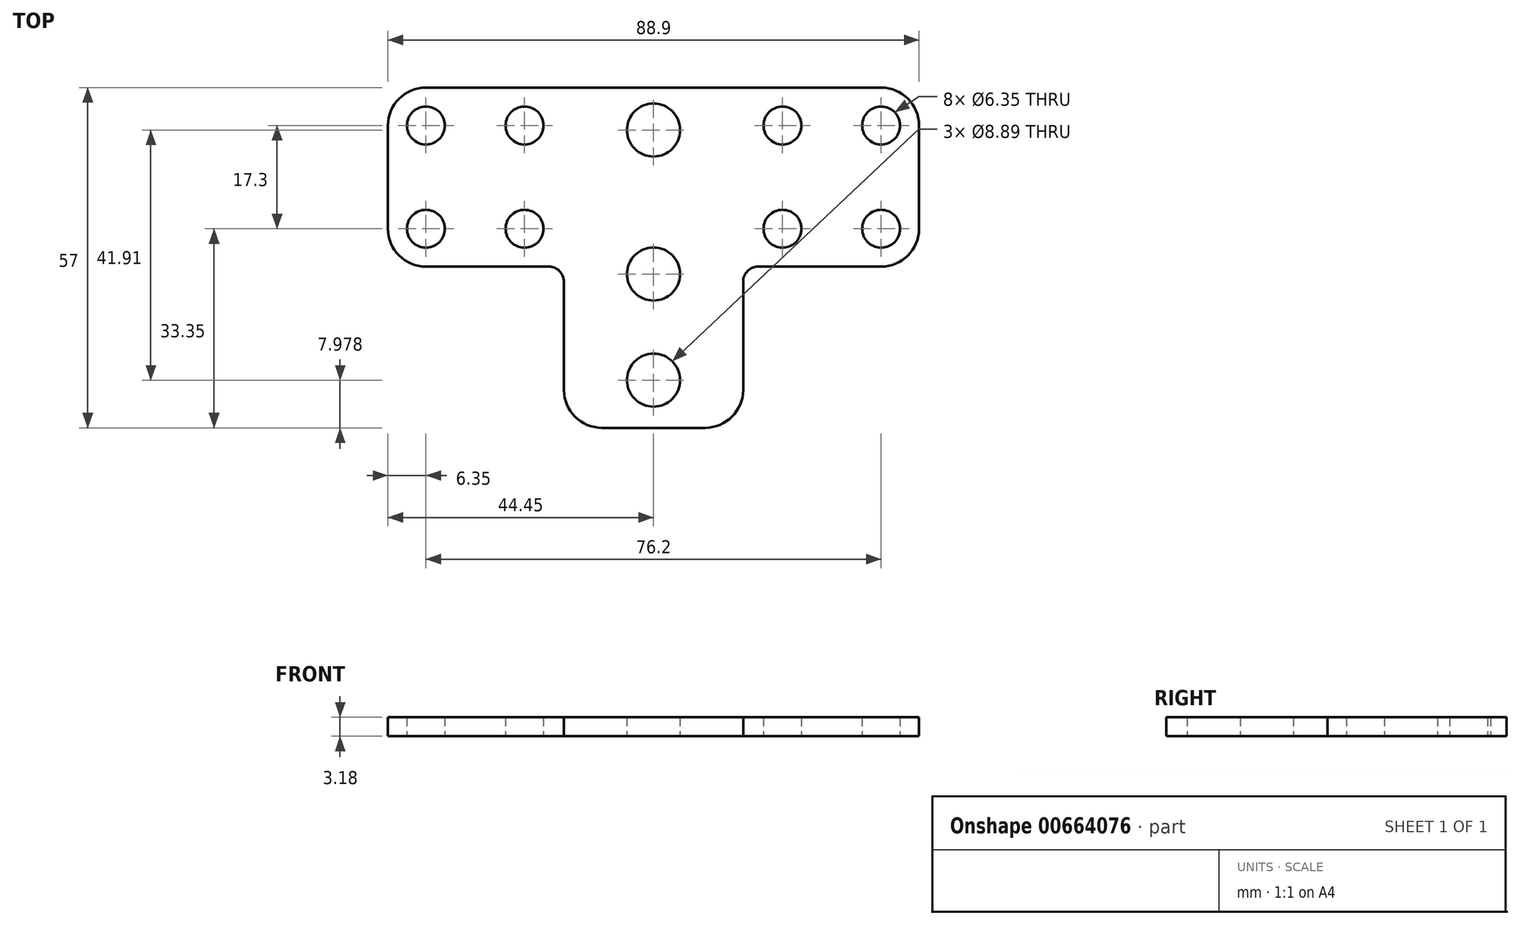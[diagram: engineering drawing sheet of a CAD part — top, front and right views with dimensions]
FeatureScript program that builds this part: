
annotation { "Feature Type Name" : "Feature", "Feature Type Description" : "" }
export const myFeature = defineFeature(function(context is Context, id is Id, definition is map)
    precondition{}
    {
        {
            var Q0;
            Q0=qCreatedBy(makeId("Top.planeOp"),FACE);
            var sketch = newSketch(context, id + "F0", { "sketchPlane" : qUnion([Q0])});
            skLineSegment(sketch, "E0.bottom", {"start": v(6.35, 0) * mm, "end": v(82.55, 0) * mm});
            skLineSegment(sketch, "E0.top", {"start": v(6.35, -30) * mm, "end": v(26.91, -30) * mm});
            skLineSegment(sketch, "E0.left", {"start": v(0, -6.35) * mm, "end": v(0, -23.65) * mm});
            skLineSegment(sketch, "E0.right", {"start": v(88.9, -6.35) * mm, "end": v(88.9, -23.65) * mm});
            skLineSegment(sketch, "E1.top", {"start": v(35.8, -57) * mm, "end": v(53.1, -57) * mm});
            skLineSegment(sketch, "E1.left", {"start": v(29.45, -32.54) * mm, "end": v(29.45, -50.65) * mm});
            skLineSegment(sketch, "E1.right", {"start": v(59.45, -32.54) * mm, "end": v(59.45, -50.65) * mm});
            skLineSegment(sketch, "E2.trimOffspring", {"start": v(61.99, -30) * mm, "end": v(82.55, -30) * mm});
            skPoint(sketch, "E3.visualSharp", {"position": v(0, 0) * mm});
            skArc(sketch, "E3.filletArc", {"start": v(6.35, 0) * mm, "mid": v(1.86, -1.86) * mm, "end": v(0, -6.35) * mm});
            skPoint(sketch, "E4.visualSharp", {"position": v(88.9, 0) * mm});
            skArc(sketch, "E4.filletArc", {"start": v(88.9, -6.35) * mm, "mid": v(87.04, -1.86) * mm, "end": v(82.55, 0) * mm});
            skPoint(sketch, "E5.visualSharp", {"position": v(0, -30) * mm});
            skArc(sketch, "E5.filletArc", {"start": v(0, -23.65) * mm, "mid": v(1.86, -28.14) * mm, "end": v(6.35, -30) * mm});
            skPoint(sketch, "E6.visualSharp", {"position": v(29.45, -30) * mm});
            skArc(sketch, "E6.filletArc", {"start": v(29.45, -32.54) * mm, "mid": v(28.7, -30.74) * mm, "end": v(26.91, -30) * mm});
            skPoint(sketch, "E7.visualSharp", {"position": v(29.45, -57) * mm});
            skArc(sketch, "E7.filletArc", {"start": v(29.45, -50.65) * mm, "mid": v(31.3, -55.14) * mm, "end": v(35.8, -57) * mm});
            skPoint(sketch, "E8.visualSharp", {"position": v(59.45, -57) * mm});
            skArc(sketch, "E8.filletArc", {"start": v(53.1, -57) * mm, "mid": v(57.6, -55.14) * mm, "end": v(59.45, -50.65) * mm});
            skPoint(sketch, "E9.visualSharp", {"position": v(59.45, -30) * mm});
            skArc(sketch, "E9.filletArc", {"start": v(61.99, -30) * mm, "mid": v(60.2, -30.74) * mm, "end": v(59.45, -32.54) * mm});
            skPoint(sketch, "E10.visualSharp", {"position": v(88.9, -30) * mm});
            skArc(sketch, "E10.filletArc", {"start": v(82.55, -30) * mm, "mid": v(87.04, -28.14) * mm, "end": v(88.9, -23.65) * mm});
            skCircle(sketch, "E11", {"center": v(6.35, -6.35) * mm, "radius": 3.18 * mm});
            skCircle(sketch, "E12", {"center": v(6.35, -23.65) * mm, "radius": 3.18 * mm});
            skCircle(sketch, "E13", {"center": v(22.86, -6.35) * mm, "radius": 3.18 * mm});
            skCircle(sketch, "E14", {"center": v(22.86, -23.65) * mm, "radius": 3.18 * mm});
            skCircle(sketch, "E15", {"center": v(44.45, -31.24) * mm, "radius": 4.45 * mm});
            skCircle(sketch, "E16", {"center": v(44.45, -49.02) * mm, "radius": 4.45 * mm});
            skLineSegment(sketch, "E17", {"start": v(44.45, -31.24) * mm, "end": v(44.45, -49.02) * mm, "construction": true});
            skCircle(sketch, "E18", {"center": v(44.45, -7.11) * mm, "radius": 4.45 * mm});
            skLineSegment(sketch, "E19", {"start": v(44.45, 0) * mm, "end": v(44.45, -7.11) * mm, "construction": true});
            skLineSegment(sketch, "E20", {"start": v(44.45, -57) * mm, "end": v(44.45, -49.02) * mm, "construction": true});
            skLineSegment(sketch, "E21", {"start": v(6.35, 0) * mm, "end": v(6.35, -6.35) * mm, "construction": true});
            skLineSegment(sketch, "E22", {"start": v(6.35, -6.35) * mm, "end": v(22.86, -6.35) * mm, "construction": true});
            skLineSegment(sketch, "E23", {"start": v(22.86, 0) * mm, "end": v(22.86, -6.35) * mm, "construction": true});
            skLineSegment(sketch, "E24", {"start": v(6.35, -6.35) * mm, "end": v(6.35, -23.65) * mm, "construction": true});
            skLineSegment(sketch, "E25", {"start": v(22.86, -6.35) * mm, "end": v(22.86, -23.65) * mm, "construction": true});
            skLineSegment(sketch, "E26", {"start": v(6.35, -23.65) * mm, "end": v(22.86, -23.65) * mm, "construction": true});
            skCircle(sketch, "E27.MirrorC", {"center": v(82.55, -6.35) * mm, "radius": 3.18 * mm});
            skCircle(sketch, "E28.MirrorC", {"center": v(66.04, -6.35) * mm, "radius": 3.18 * mm});
            skCircle(sketch, "E29.MirrorC", {"center": v(66.04, -23.65) * mm, "radius": 3.18 * mm});
            skCircle(sketch, "E30.MirrorC", {"center": v(82.55, -23.65) * mm, "radius": 3.18 * mm});
            skLineSegment(sketch, "E31", {"start": v(44.45, -7.11) * mm, "end": v(44.45, -31.24) * mm});
            skSolve(sketch);
        }
        {
            var Q0;
            Q0=makeQuery(id+"F0.imprint","IMPRINT",FACE,{"disambiguationData":[TD([[makeQuery(id+"F0.imprint","IMPRINT",EDGE,{"derivedFrom":sQuery(id+"F0.wireOp",EDGE,"E0.bottom")}),-1.0]])]});
            extrude(context, id + "F1", {"entities" : qUnion([Q0]), "depth" : 3.17 * mm, "offsetDistance" : 25.4 * mm});
        }
    });
